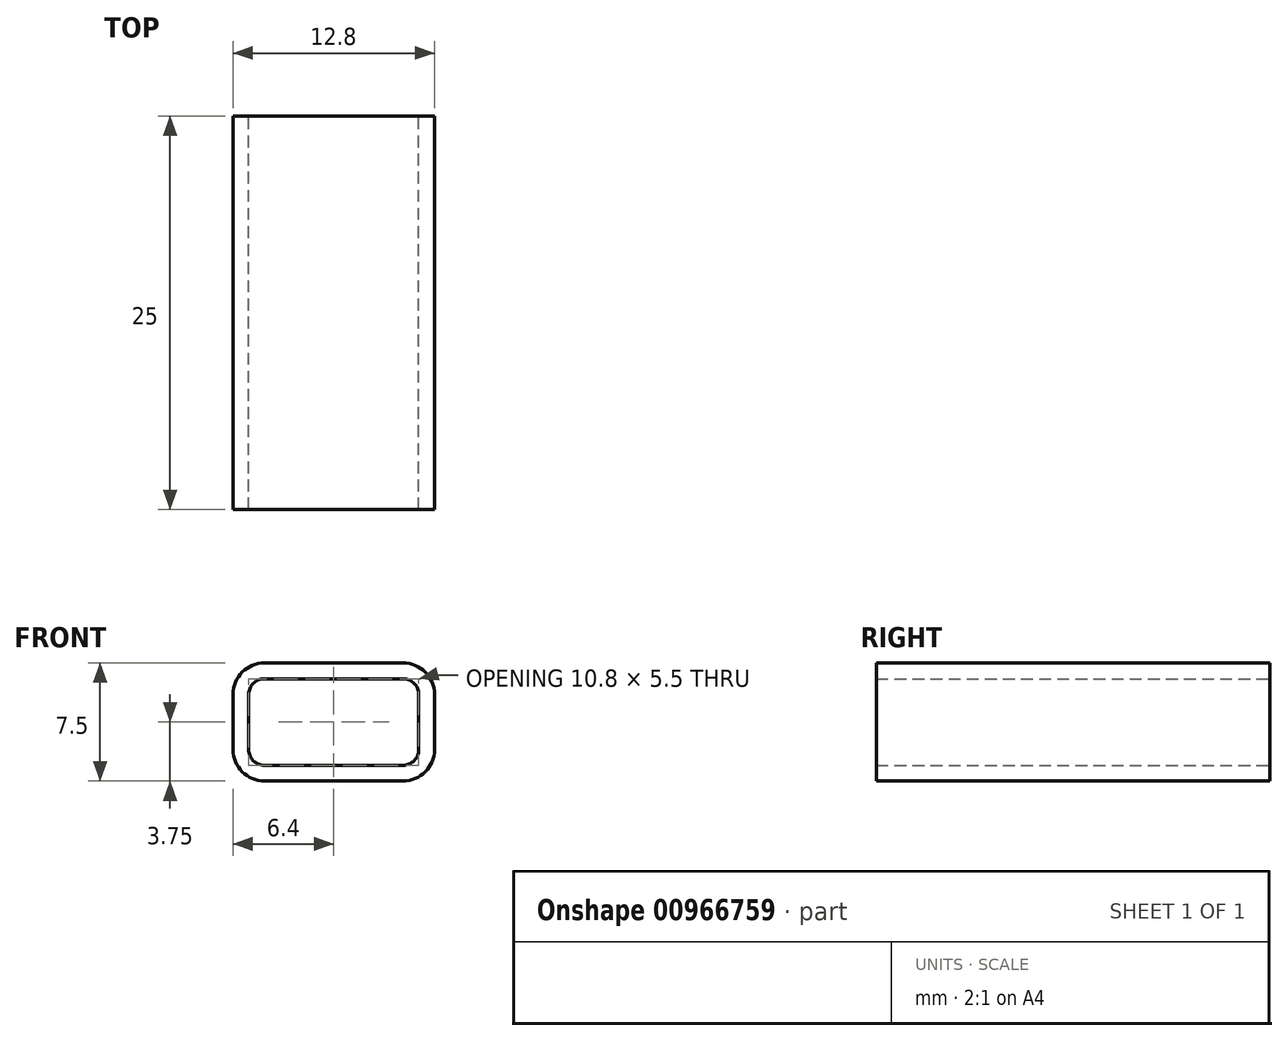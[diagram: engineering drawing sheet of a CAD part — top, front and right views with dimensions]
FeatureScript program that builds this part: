
annotation { "Feature Type Name" : "Feature", "Feature Type Description" : "" }
export const myFeature = defineFeature(function(context is Context, id is Id, definition is map)
    precondition{}
    {
        {
            var Q0;
            Q0=qCreatedBy(makeId("Front.planeOp"),FACE);
            var sketch = newSketch(context, id + "F0", { "sketchPlane" : qUnion([Q0])});
            skLineSegment(sketch, "E0.bottom", {"start": v(4.4, -2.75) * mm, "end": v(-4.4, -2.75) * mm});
            skLineSegment(sketch, "E0.top", {"start": v(4.4, 2.75) * mm, "end": v(-4.4, 2.75) * mm});
            skLineSegment(sketch, "E0.left", {"start": v(5.4, -1.75) * mm, "end": v(5.4, 1.75) * mm});
            skLineSegment(sketch, "E0.right", {"start": v(-5.4, -1.75) * mm, "end": v(-5.4, 1.75) * mm});
            skPoint(sketch, "E0.middle", {"position": v(0, 0) * mm});
            skPoint(sketch, "E1.visualSharp", {"position": v(-5.4, 2.75) * mm});
            skArc(sketch, "E1.filletArc", {"start": v(-4.4, 2.75) * mm, "mid": v(-5.1, 2.46) * mm, "end": v(-5.4, 1.75) * mm});
            skPoint(sketch, "E2.visualSharp", {"position": v(5.4, 2.75) * mm});
            skArc(sketch, "E2.filletArc", {"start": v(5.4, 1.75) * mm, "mid": v(5.1, 2.46) * mm, "end": v(4.4, 2.75) * mm});
            skPoint(sketch, "E3.visualSharp", {"position": v(5.4, -2.75) * mm});
            skArc(sketch, "E3.filletArc", {"start": v(4.4, -2.75) * mm, "mid": v(5.1, -2.46) * mm, "end": v(5.4, -1.75) * mm});
            skPoint(sketch, "E4.visualSharp", {"position": v(-5.4, -2.75) * mm});
            skArc(sketch, "E4.filletArc", {"start": v(-5.4, -1.75) * mm, "mid": v(-5.1, -2.46) * mm, "end": v(-4.4, -2.75) * mm});
            skArc(sketch, "E5.0", {"start": v(6.4, 1.75) * mm, "mid": v(5.81, 3.16) * mm, "end": v(4.4, 3.75) * mm});
            skLineSegment(sketch, "E5.1", {"start": v(6.4, -1.75) * mm, "end": v(6.4, 1.75) * mm});
            skLineSegment(sketch, "E5.2", {"start": v(4.4, 3.75) * mm, "end": v(-4.4, 3.75) * mm});
            skArc(sketch, "E5.3", {"start": v(4.4, -3.75) * mm, "mid": v(5.81, -3.16) * mm, "end": v(6.4, -1.75) * mm});
            skArc(sketch, "E5.4", {"start": v(-4.4, 3.75) * mm, "mid": v(-5.81, 3.16) * mm, "end": v(-6.4, 1.75) * mm});
            skLineSegment(sketch, "E5.5", {"start": v(-6.4, -1.75) * mm, "end": v(-6.4, 1.75) * mm});
            skArc(sketch, "E5.6", {"start": v(-6.4, -1.75) * mm, "mid": v(-5.81, -3.16) * mm, "end": v(-4.4, -3.75) * mm});
            skLineSegment(sketch, "E5.7", {"start": v(4.4, -3.75) * mm, "end": v(-4.4, -3.75) * mm});
            skSolve(sketch);
        }
        {
            var Q0;
            Q0=makeQuery(id+"F0.imprint","IMPRINT",FACE,{"disambiguationData":[TD([[makeQuery(id+"F0.imprint","IMPRINT",EDGE,{"derivedFrom":sQuery(id+"F0.wireOp",EDGE,"E0.bottom")}),1.0]])]});
            extrude(context, id + "F1", {"entities" : qUnion([Q0]), "depth" : 25 * mm, "offsetDistance" : 25 * mm});
        }
    });
